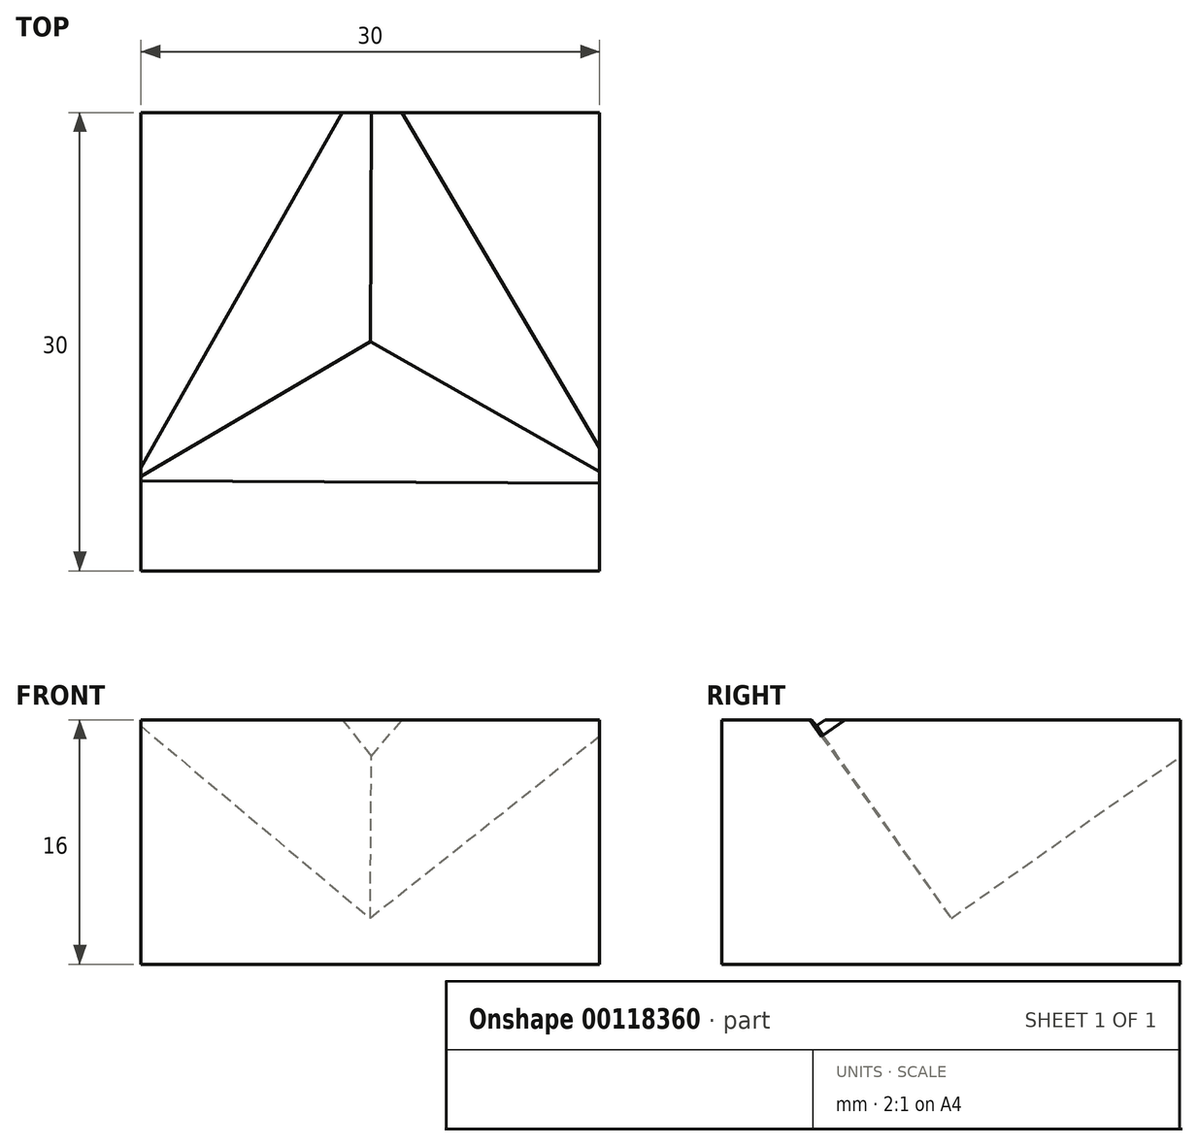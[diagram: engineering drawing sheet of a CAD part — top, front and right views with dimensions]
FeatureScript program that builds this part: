
annotation { "Feature Type Name" : "Feature", "Feature Type Description" : "" }
export const myFeature = defineFeature(function(context is Context, id is Id, definition is map)
    precondition{}
    {
        {
            var Q0;
            Q0=qCreatedBy(makeId("Top.planeOp"),FACE);
            var sketch = newSketch(context, id + "F0", { "sketchPlane" : qUnion([Q0])});
            skLineSegment(sketch, "E0.bottom", {"start": v(-30, 30) * mm, "end": v(0, 30) * mm});
            skLineSegment(sketch, "E0.top", {"start": v(-30, 0) * mm, "end": v(0, 0) * mm});
            skLineSegment(sketch, "E0.left", {"start": v(-30, 30) * mm, "end": v(-30, 0) * mm});
            skLineSegment(sketch, "E0.right", {"start": v(0, 30) * mm, "end": v(0, 0) * mm});
            skSolve(sketch);
        }
        {
            var Q0;
            Q0=makeQuery(id+"F0.imprint","IMPRINT",FACE,{"disambiguationData":[TD([[makeQuery(id+"F0.imprint","IMPRINT",EDGE,{"derivedFrom":sQuery(id+"F0.wireOp",EDGE,"E0.bottom")}),-1.0]])]});
            extrude(context, id + "F1", {"entities" : qUnion([Q0]), "depth" : 16 * mm});
        }
        {
            var Q0;
            Q0=makeQuery(id+"F1.opExtrude","SWEPT_FACE",FACE,{"disambiguationData":[OSD([sQuery(id+"F0.wireOp",EDGE,"E0.right")])]});
            var sketch = newSketch(context, id + "F2", { "sketchPlane" : qUnion([Q0])});
            skLineSegment(sketch, "E1", {"start": v(15, 0) * mm, "end": v(32.68, 17.68) * mm});
            skLineSegment(sketch, "E2", {"start": v(32.68, 17.68) * mm, "end": v(15, 35.36) * mm});
            skLineSegment(sketch, "E3", {"start": v(15, 35.36) * mm, "end": v(-2.68, 17.68) * mm});
            skLineSegment(sketch, "E4", {"start": v(-2.68, 17.68) * mm, "end": v(15, 0) * mm});
            skLineSegment(sketch, "E5", {"start": v(-2.68, 17.68) * mm, "end": v(32.68, 17.68) * mm, "construction": true});
            skSolve(sketch);
        }
        {
            var Q0;
            {var subQ6=sQuery(id+"F2.wireOp",EDGE,"E2");Q0=makeQuery(id+"F2.imprint","IMPRINT",FACE,{"disambiguationData":[TD([[makeQuery(id+"F2.imprint","IMPRINT",EDGE,{"derivedFrom":subQ6}),1.0]])]});}
            var Q1;
            {var subQ0=sQuery(id+"F0.wireOp",EDGE,"E0.right");var subQ1=makeQuery(id+"F1.opExtrude","CAP_EDGE",EDGE,{"disambiguationData":[OSD([subQ0])],"isStart":false});Q1=makeQuery(id+"F2.imprint","IMPRINT",FACE,{"disambiguationData":[TD([[makeQuery(id+"F2.imprint","IMPRINT",EDGE,{"derivedFrom":subQ1}),1.0]])]});}
            extrude(context, id + "F3", {"entities" : qUnion([Q0, Q1]), "depth" : 25 * mm});
        }
        {
            var Q0;
            Q0=makeQuery(id+"F3.opExtrude","SWEPT_BODY",BODY,{"disambiguationData":[OSD([sQuery(id+"F2.wireOp",EDGE,"E1"),sQuery(id+"F2.wireOp",EDGE,"E2"),sQuery(id+"F2.wireOp",EDGE,"E3"),sQuery(id+"F2.wireOp",EDGE,"E4")])]});
            var Q1;
            Q1=makeQuery(id+"F3.opExtrude","SWEPT_EDGE",EDGE,{"disambiguationData":[OSD([sQuery(id+"F0.wireOp",EDGE,"E0.right"),sQuery(id+"F2.wireOp",EDGE,"E1"),sQuery(id+"F2.wireOp",EDGE,"E4")])]});
            transform(context, id + "F4", {"entities" : qUnion([Q0]), "transformType" : TransformType.ROTATION, "transformAxis" : qUnion([Q1]), "angle" : 45 * degree, "makeCopy" : false});
        }
        {
            var Q0;
            Q0=makeQuery(id+"F3.opExtrude","SWEPT_BODY",BODY,{"disambiguationData":[OSD([sQuery(id+"F2.wireOp",EDGE,"E1"),sQuery(id+"F2.wireOp",EDGE,"E2"),sQuery(id+"F2.wireOp",EDGE,"E3"),sQuery(id+"F2.wireOp",EDGE,"E4")])]});
            var Q1;
            Q1=makeQuery(id+"F3.opExtrude","CAP_EDGE",EDGE,{"disambiguationData":[OSD([sQuery(id+"F2.wireOp",EDGE,"E1")])],"isStart":true});
            transform(context, id + "F5", {"entities" : qUnion([Q0]), "transformType" : TransformType.ROTATION, "transformAxis" : qUnion([Q1]), "angle" : 45 * degree, "oppositeDirection" : true, "makeCopy" : false});
        }
        {
            var Q0;
            Q0=makeQuery(id+"F0.imprint","IMPRINT",FACE,{"disambiguationData":[TD([[makeQuery(id+"F0.imprint","IMPRINT",EDGE,{"derivedFrom":sQuery(id+"F0.wireOp",EDGE,"E0.bottom")}),-1.0]])]});
            var sketch = newSketch(context, id + "F6", { "sketchPlane" : qUnion([Q0])});
            skLineSegment(sketch, "E6.0", {"start": v(0, 30) * mm, "end": v(0, 0) * mm, "construction": true});
            skLineSegment(sketch, "E6.1", {"start": v(-30, 30) * mm, "end": v(-30, 0) * mm, "construction": true});
            skLineSegment(sketch, "E7", {"start": v(-30, 14.35) * mm, "end": v(0, 15) * mm, "construction": true});
            skLineSegment(sketch, "E8.0", {"start": v(-30, 0) * mm, "end": v(0, 0) * mm, "construction": true});
            skLineSegment(sketch, "E9.0", {"start": v(-30, 30) * mm, "end": v(0, 30) * mm, "construction": true});
            skLineSegment(sketch, "E10", {"start": v(-15, 0) * mm, "end": v(-15, 14.68) * mm, "construction": true});
            skLineSegment(sketch, "E11", {"start": v(-15, 7.34) * mm, "end": v(0, 7.34) * mm, "construction": true});
            skSolve(sketch);
        }
        {
            var Q0;
            Q0=makeQuery(id+"F3.opExtrude","SWEPT_BODY",BODY,{"disambiguationData":[OSD([sQuery(id+"F2.wireOp",EDGE,"E1"),sQuery(id+"F2.wireOp",EDGE,"E2"),sQuery(id+"F2.wireOp",EDGE,"E3"),sQuery(id+"F2.wireOp",EDGE,"E4")])]});
            var Q1;
            Q1=sQuery(id+"F6.wireOp",EDGE,"E7");
            transform(context, id + "F7", {"entities" : qUnion([Q0]), "transformType" : TransformType.ROTATION, "transformAxis" : qUnion([Q1]), "angle" : 35.26 * degree, "makeCopy" : false});
        }
        {
            var Q0;
            Q0=makeQuery(id+"F3.opExtrude","SWEPT_BODY",BODY,{"disambiguationData":[OSD([sQuery(id+"F2.wireOp",EDGE,"E1"),sQuery(id+"F2.wireOp",EDGE,"E2"),sQuery(id+"F2.wireOp",EDGE,"E3"),sQuery(id+"F2.wireOp",EDGE,"E4")])]});
            var Q1;
            Q1=sQuery(id+"F6.wireOp",EDGE,"E11");
            transform(context, id + "F8", {"entities" : qUnion([Q0]), "transformType" : TransformType.TRANSLATION_ENTITY, "oppositeDirectionEntity" : true, "transformLine" : qUnion([Q1]), "makeCopy" : false});
        }
        {
            var Q0;
            Q0=makeQuery(id+"F1.opExtrude","SWEPT_FACE",FACE,{"disambiguationData":[OSD([sQuery(id+"F0.wireOp",EDGE,"E0.right")])]});
            var sketch = newSketch(context, id + "F9", { "sketchPlane" : qUnion([Q0])});
            skLineSegment(sketch, "E12", {"start": v(15, 0) * mm, "end": v(15, 3) * mm, "construction": true});
            skSolve(sketch);
        }
        {
            var Q0;
            Q0=makeQuery(id+"F3.opExtrude","SWEPT_BODY",BODY,{"disambiguationData":[OSD([sQuery(id+"F2.wireOp",EDGE,"E1"),sQuery(id+"F2.wireOp",EDGE,"E2"),sQuery(id+"F2.wireOp",EDGE,"E3"),sQuery(id+"F2.wireOp",EDGE,"E4")])]});
            var Q1;
            Q1=sQuery(id+"F9.wireOp",EDGE,"E12");
            transform(context, id + "F10", {"entities" : qUnion([Q0]), "transformType" : TransformType.TRANSLATION_ENTITY, "oppositeDirectionEntity" : false, "transformLine" : qUnion([Q1]), "makeCopy" : false});
        }
        {
            var Q0;
            Q0=makeQuery(id+"F3.opExtrude","SWEPT_BODY",BODY,{"disambiguationData":[OSD([sQuery(id+"F2.wireOp",EDGE,"E1"),sQuery(id+"F2.wireOp",EDGE,"E2"),sQuery(id+"F2.wireOp",EDGE,"E3"),sQuery(id+"F2.wireOp",EDGE,"E4")])]});
            var Q1;
            Q1=makeQuery(id+"F1.opExtrude","SWEPT_BODY",BODY,{"disambiguationData":[OSD([sQuery(id+"F0.wireOp",EDGE,"E0.bottom"),sQuery(id+"F0.wireOp",EDGE,"E0.top"),sQuery(id+"F0.wireOp",EDGE,"E0.left"),sQuery(id+"F0.wireOp",EDGE,"E0.right")])]});
            booleanBodies(context, id + "F11", {"operationType" : BooleanOperationType.SUBTRACTION, "tools" : qUnion([Q0]), "targets" : qUnion([Q1])});
        }
    });
